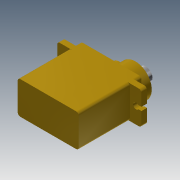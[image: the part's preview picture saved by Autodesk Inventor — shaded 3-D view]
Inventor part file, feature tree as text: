
AUTODESK INVENTOR PART (.ipt)
format: ipt  version: 2013 (Build 170138000, 138)  size: 222,208 bytes
history: native  units: mm
features: sketch x17, fillet x12, extrude x11
ambient origin geometry x8: Origin, YZ Plane, XZ Plane, XY Plane, X Axis, Y Axis, Z Axis, Center Point
bodies: Solid1 (feature_tree)
feature tree (40):
  extrude  "Extrusion1"  Depth=4.4mm TaperAngle=0.0deg
  sketch  "Sketch2"  dims[d11=4.4mm d12=0.0mm d18=7.9mm d19=0.0mm]
  sketch  "Sketch6"  dims[d20=7.9mm d21=0.0mm d22=7.9mm d23=0.0mm]
  extrude  "Extrusion2"  Depth=7.9mm TaperAngle=0.0deg
  sketch  "Sketch7"  dims[d26=4.0mm d27=0.0mm d28=5.0mm]
  sketch  "Sketch8"  dims[d29=3.0mm d30=0.0mm d31=3.0mm d32=0.0mm]
  sketch  "Sketch9"  dims[d39=3.0mm d40=0.0mm d43=3.0mm d44=0.0mm]
  extrude  "Extrusion3"  Depth=7.9mm TaperAngle=0.0deg
  sketch  "Sketch10"  dims[d45=1.0mm d46=1.0mm]
  sketch  "Sketch11"  dims[d47=1.0mm d48=1.0mm]
  extrude  "Extrusion4"  Depth=5.0mm
  extrude  "Extrusion5"  Depth=3.0mm TaperAngle=0.0deg
  extrude  "Extrusion6"  Depth=3.0mm TaperAngle=0.0deg
  extrude  "Extrusion7"  Depth=1.0mm
  extrude  "Extrusion8"  Depth=1.0mm
  extrude  "Extrusion9"  Depth=1.0mm
  sketch  "Sketch16"
  sketch  "Sketch17"
  sketch  "Sketch18"
  sketch  "Sketch19"
  extrude  "Extrusion10"  Depth=1.0mm
  extrude  "Extrusion11"  Depth=1.0mm
  fillet  "Fillet1"  Radius=1.0mm
  sketch  "Sketch20"
  fillet  "Fillet2"  Radius=1.0mm
  fillet  "Fillet3"  [1 undecoded]
  fillet  "Fillet4"  [1 undecoded]
  fillet  "Fillet5"  [1 undecoded]
  fillet  "Fillet6"  [1 undecoded]
  fillet  "Fillet7"  [1 undecoded]
  fillet  "Fillet8"  [1 undecoded]
  fillet  "Fillet9"  [1 undecoded]
  fillet  "Fillet10"  [1 undecoded]
  fillet  "Fillet11"  [1 undecoded]
  fillet  "Fillet12"  [1 undecoded]
  sketch  "Sketch1"  dims[d2=31.7mm d3=0.0mm d7=4.4mm d8=0.0mm]
  sketch  "Sketch12"  dims[d49=1.0mm d50=1.0mm]
  sketch  "Sketch13"  dims[d51=1.0mm d52=1.0mm]
  sketch  "Sketch14"  dims[d53=1.0mm d54=1.0mm d55=1.0mm d56=1.0mm]
  sketch  "Sketch15"
note: 10 required parameter values undecoded (feature->parameter linkage not recoverable at this tier; creation-order binding heuristic only, values carry confidence <= 0.55)
